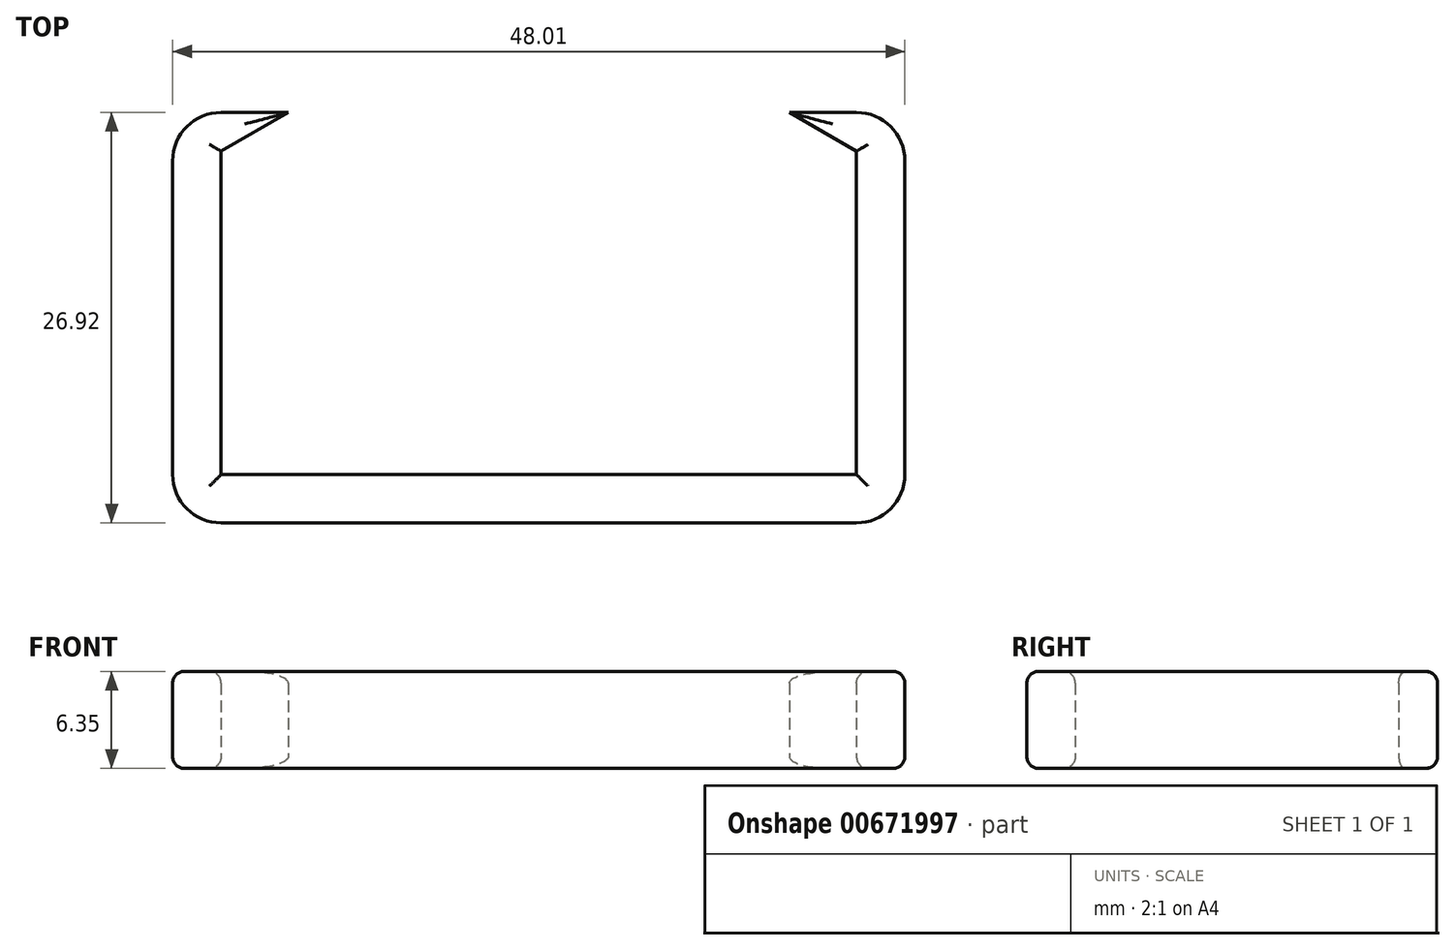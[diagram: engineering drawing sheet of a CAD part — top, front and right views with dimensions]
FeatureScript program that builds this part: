
annotation { "Feature Type Name" : "Feature", "Feature Type Description" : "" }
export const myFeature = defineFeature(function(context is Context, id is Id, definition is map)
    precondition{}
    {
        {
            var Q0;
            Q0=qCreatedBy(makeId("Top.planeOp"),FACE);
            var sketch = newSketch(context, id + "F0", { "sketchPlane" : qUnion([Q0])});
            skLineSegment(sketch, "E0", {"start": v(-16.17, 0) * mm, "end": v(-20.57, 0) * mm});
            skLineSegment(sketch, "E1", {"start": v(-23.75, -3.18) * mm, "end": v(-23.75, -23.75) * mm});
            skLineSegment(sketch, "E2", {"start": v(-20.57, -26.92) * mm, "end": v(21.08, -26.92) * mm});
            skLineSegment(sketch, "E3", {"start": v(24.26, -23.75) * mm, "end": v(24.26, -3.17) * mm});
            skLineSegment(sketch, "E4", {"start": v(21.08, 0) * mm, "end": v(16.68, 0) * mm});
            skLineSegment(sketch, "E5", {"start": v(16.68, 0) * mm, "end": v(21.08, -2.54) * mm});
            skLineSegment(sketch, "E6", {"start": v(21.08, -2.54) * mm, "end": v(21.08, -23.75) * mm});
            skLineSegment(sketch, "E7", {"start": v(21.08, -23.75) * mm, "end": v(-20.57, -23.75) * mm});
            skLineSegment(sketch, "E8", {"start": v(-20.57, -23.75) * mm, "end": v(-20.57, -2.54) * mm});
            skLineSegment(sketch, "E9", {"start": v(-20.57, -2.54) * mm, "end": v(-16.17, 0) * mm});
            skPoint(sketch, "E10.visualSharp", {"position": v(-23.75, -26.92) * mm});
            skArc(sketch, "E10.filletArc", {"start": v(-23.75, -23.75) * mm, "mid": v(-22.82, -26) * mm, "end": v(-20.57, -26.92) * mm});
            skPoint(sketch, "E11.visualSharp", {"position": v(24.26, -26.92) * mm});
            skArc(sketch, "E11.filletArc", {"start": v(21.08, -26.92) * mm, "mid": v(23.33, -26) * mm, "end": v(24.26, -23.75) * mm});
            skPoint(sketch, "E12.visualSharp", {"position": v(24.26, 0) * mm});
            skArc(sketch, "E12.filletArc", {"start": v(24.26, -3.17) * mm, "mid": v(23.33, -0.93) * mm, "end": v(21.08, 0) * mm});
            skPoint(sketch, "E13.visualSharp", {"position": v(-23.75, 0) * mm});
            skArc(sketch, "E13.filletArc", {"start": v(-20.57, 0) * mm, "mid": v(-22.82, -0.93) * mm, "end": v(-23.75, -3.18) * mm});
            skSolve(sketch);
        }
        {
            var Q0;
            Q0 = qSketchRegion(id + "F0", true);
            extrude(context, id + "F1", {"entities" : qUnion([Q0]), "depth" : 6.35 * mm, "offsetDistance" : 25.4 * mm});
        }
        {
            var Q0;
            Q0=makeQuery(id+"F1.opExtrude","CAP_FACE",FACE,{"disambiguationData":[OSD([sQuery(id+"F0.wireOp",EDGE,"E0"),sQuery(id+"F0.wireOp",EDGE,"E1"),sQuery(id+"F0.wireOp",EDGE,"E2"),sQuery(id+"F0.wireOp",EDGE,"E3"),sQuery(id+"F0.wireOp",EDGE,"E4"),sQuery(id+"F0.wireOp",EDGE,"E5"),sQuery(id+"F0.wireOp",EDGE,"E6"),sQuery(id+"F0.wireOp",EDGE,"E7"),sQuery(id+"F0.wireOp",EDGE,"E8"),sQuery(id+"F0.wireOp",EDGE,"E9"),sQuery(id+"F0.wireOp",EDGE,"E10.filletArc"),sQuery(id+"F0.wireOp",EDGE,"E11.filletArc"),sQuery(id+"F0.wireOp",EDGE,"E12.filletArc"),sQuery(id+"F0.wireOp",EDGE,"E13.filletArc")])],"isStart":false});
            var Q1;
            Q1=makeQuery(id+"F1.opExtrude","CAP_FACE",FACE,{"disambiguationData":[OSD([sQuery(id+"F0.wireOp",EDGE,"E0"),sQuery(id+"F0.wireOp",EDGE,"E1"),sQuery(id+"F0.wireOp",EDGE,"E2"),sQuery(id+"F0.wireOp",EDGE,"E3"),sQuery(id+"F0.wireOp",EDGE,"E4"),sQuery(id+"F0.wireOp",EDGE,"E5"),sQuery(id+"F0.wireOp",EDGE,"E6"),sQuery(id+"F0.wireOp",EDGE,"E7"),sQuery(id+"F0.wireOp",EDGE,"E8"),sQuery(id+"F0.wireOp",EDGE,"E9"),sQuery(id+"F0.wireOp",EDGE,"E10.filletArc"),sQuery(id+"F0.wireOp",EDGE,"E11.filletArc"),sQuery(id+"F0.wireOp",EDGE,"E12.filletArc"),sQuery(id+"F0.wireOp",EDGE,"E13.filletArc")])],"isStart":true});
            fillet(context, id + "F2", {"entities" : qUnion([Q0, Q1]), "radius" : 0.76 * mm, "tangentPropagation" : true, "allowEdgeOverflow" : false});
        }
    });
